# Revit family: Shower-Shower_Door-STERLING-Deluxe-572115
name_source: partatom
category: Specialty Equipment
units: mm (PartAtom-declared; Revit-internal decimal feet)

## family parameters
Cut with Voids When Loaded = No
Host = Face
OmniClass Number = 23.31.17.17
OmniClass Title = Shower Enclosures
Part Type = Normal
Room Calculation Point = No
Round Connector Dimension = Use Diameter
Shared = No

## types (4) — shared parameters
ADA Compliant = No
Assembly Code = C1030200
Date Modified = 01/12/2023
Default Elevation = 4"
Description = Bypass Door 59.375W X 69.938H
Height = 70"
Length = 4"
Manufacturer = Sterling Co.
Master Format 2014 = 10 28 19.16
Master Format 2014 Name = Shower Doors
Material = Premium Metal Construction
Product Documentation Link = https://resources.kohler.com
Product Name = Deluxe
Product Page URL = http://www.sterlingplumbing.com
URL = https://www.sterlingplumbing.com
WaterSense Certified = No

## per-type parameters (varying)
| type | Finish | Model | Secondary Finish | Type |
| Clear Glass Texture, S-Silver | Sterling-Metal-S-Silver | 572115-G05-S | Sterling-Glass-G05-Clear_Glass_Texture | 1 |
| Clear Glass Texture, N-Nickel | Sterling-Metal-N-Nickel | 572115-G05-N | Sterling-Glass-G05-Clear_Glass_Texture | 2 |
| Pebbled Glass Texture, N-Nickel | Sterling-Metal-N-Nickel | 572115-G10-N | Sterling-Glass-G10-Pebbled_Glass_Texture | 3 |
| Rain Glass Texture, S-Silver | Sterling-Metal-S-Silver | 572115-3G06-S | Sterling-Glass-G06-Rain_Glass_Texture | 4 |

## geometry (parser evidence)
native form markers: Sweep x5
no freeform markers — native parametric forms only
